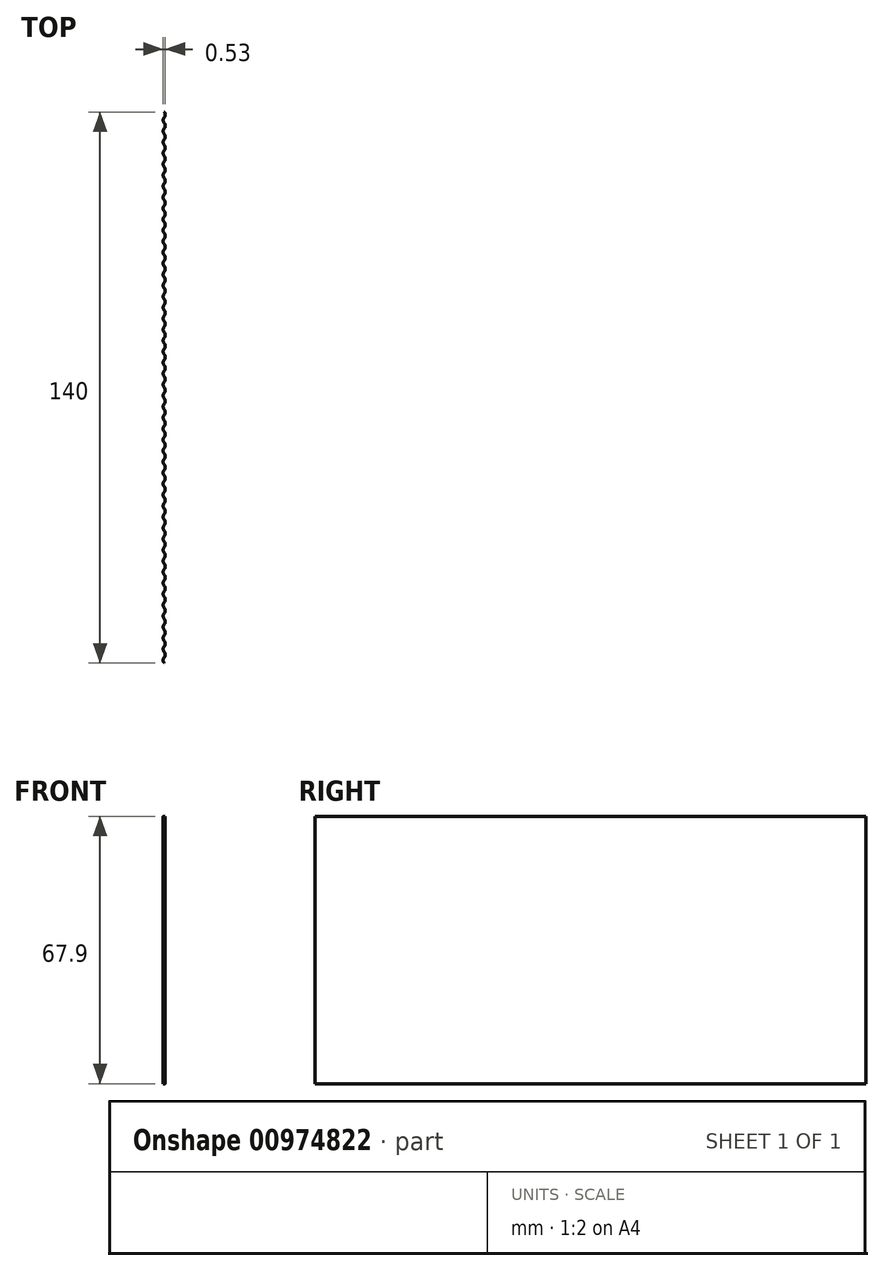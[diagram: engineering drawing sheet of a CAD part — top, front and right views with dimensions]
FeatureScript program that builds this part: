
annotation { "Feature Type Name" : "Feature", "Feature Type Description" : "" }
export const myFeature = defineFeature(function(context is Context, id is Id, definition is map)
    precondition{}
    {
        {
            var Q0;
            Q0=qCreatedBy(makeId("Top.planeOp"),FACE);
            var sketch = newSketch(context, id + "F0", { "sketchPlane" : qUnion([Q0])});
            skArc(sketch, "E0", {"start": v(0, 1.4) * mm, "mid": v(-0.25, 0.7) * mm, "end": v(0, 0) * mm});
            skArc(sketch, "E1", {"start": v(0, 1.4) * mm, "mid": v(0.25, 2.1) * mm, "end": v(0, 2.8) * mm});
            skArc(sketch, "E2.1.0.0", {"start": v(0.03, 1.4) * mm, "mid": v(0.28, 2.1) * mm, "end": v(0.03, 2.8) * mm});
            skArc(sketch, "E2.1.0.1", {"start": v(0.03, 1.4) * mm, "mid": v(-0.22, 0.7) * mm, "end": v(0.03, 0) * mm});
            skLineSegment(sketch, "E2.direction1", {"start": v(0, 0) * mm, "end": v(0.03, 0) * mm, "construction": true});
            skArc(sketch, "E3.0.1.0", {"start": v(0.03, 4.2) * mm, "mid": v(0.28, 4.9) * mm, "end": v(0.03, 5.6) * mm});
            skArc(sketch, "E3.0.1.1", {"start": v(0, 4.2) * mm, "mid": v(-0.25, 3.5) * mm, "end": v(0, 2.8) * mm});
            skArc(sketch, "E3.0.1.2", {"start": v(0.03, 4.2) * mm, "mid": v(-0.22, 3.5) * mm, "end": v(0.03, 2.8) * mm});
            skArc(sketch, "E3.0.1.3", {"start": v(0, 4.2) * mm, "mid": v(0.25, 4.9) * mm, "end": v(0, 5.6) * mm});
            skLineSegment(sketch, "E3.0.1.4", {"start": v(0, 2.8) * mm, "end": v(0.03, 2.8) * mm, "construction": true});
            skArc(sketch, "E3.0.2.0", {"start": v(0.03, 7) * mm, "mid": v(0.28, 7.7) * mm, "end": v(0.03, 8.4) * mm});
            skArc(sketch, "E3.0.2.1", {"start": v(0, 7) * mm, "mid": v(-0.25, 6.3) * mm, "end": v(0, 5.6) * mm});
            skArc(sketch, "E3.0.2.2", {"start": v(0.03, 7) * mm, "mid": v(-0.22, 6.3) * mm, "end": v(0.03, 5.6) * mm});
            skArc(sketch, "E3.0.2.3", {"start": v(0, 7) * mm, "mid": v(0.25, 7.7) * mm, "end": v(0, 8.4) * mm});
            skLineSegment(sketch, "E3.0.2.4", {"start": v(0, 5.6) * mm, "end": v(0.03, 5.6) * mm, "construction": true});
            skArc(sketch, "E3.0.3.0", {"start": v(0.03, 9.8) * mm, "mid": v(0.28, 10.5) * mm, "end": v(0.03, 11.2) * mm});
            skArc(sketch, "E3.0.3.1", {"start": v(0, 9.8) * mm, "mid": v(-0.25, 9.1) * mm, "end": v(0, 8.4) * mm});
            skArc(sketch, "E3.0.3.2", {"start": v(0.03, 9.8) * mm, "mid": v(-0.22, 9.1) * mm, "end": v(0.03, 8.4) * mm});
            skArc(sketch, "E3.0.3.3", {"start": v(0, 9.8) * mm, "mid": v(0.25, 10.5) * mm, "end": v(0, 11.2) * mm});
            skLineSegment(sketch, "E3.0.3.4", {"start": v(0, 8.4) * mm, "end": v(0.03, 8.4) * mm, "construction": true});
            skArc(sketch, "E3.0.4.0", {"start": v(0.03, 12.6) * mm, "mid": v(0.28, 13.3) * mm, "end": v(0.03, 14) * mm});
            skArc(sketch, "E3.0.4.1", {"start": v(0, 12.6) * mm, "mid": v(-0.25, 11.9) * mm, "end": v(0, 11.2) * mm});
            skArc(sketch, "E3.0.4.2", {"start": v(0.03, 12.6) * mm, "mid": v(-0.22, 11.9) * mm, "end": v(0.03, 11.2) * mm});
            skArc(sketch, "E3.0.4.3", {"start": v(0, 12.6) * mm, "mid": v(0.25, 13.3) * mm, "end": v(0, 14) * mm});
            skLineSegment(sketch, "E3.0.4.4", {"start": v(0, 11.2) * mm, "end": v(0.03, 11.2) * mm, "construction": true});
            skArc(sketch, "E3.0.5.0", {"start": v(0.03, 15.4) * mm, "mid": v(0.28, 16.1) * mm, "end": v(0.03, 16.8) * mm});
            skArc(sketch, "E3.0.5.1", {"start": v(0, 15.4) * mm, "mid": v(-0.25, 14.7) * mm, "end": v(0, 14) * mm});
            skArc(sketch, "E3.0.5.2", {"start": v(0.03, 15.4) * mm, "mid": v(-0.22, 14.7) * mm, "end": v(0.03, 14) * mm});
            skArc(sketch, "E3.0.5.3", {"start": v(0, 15.4) * mm, "mid": v(0.25, 16.1) * mm, "end": v(0, 16.8) * mm});
            skLineSegment(sketch, "E3.0.5.4", {"start": v(0, 14) * mm, "end": v(0.03, 14) * mm, "construction": true});
            skArc(sketch, "E3.0.6.0", {"start": v(0.03, 18.2) * mm, "mid": v(0.28, 18.9) * mm, "end": v(0.03, 19.6) * mm});
            skArc(sketch, "E3.0.6.1", {"start": v(0, 18.2) * mm, "mid": v(-0.25, 17.5) * mm, "end": v(0, 16.8) * mm});
            skArc(sketch, "E3.0.6.2", {"start": v(0.03, 18.2) * mm, "mid": v(-0.22, 17.5) * mm, "end": v(0.03, 16.8) * mm});
            skArc(sketch, "E3.0.6.3", {"start": v(0, 18.2) * mm, "mid": v(0.25, 18.9) * mm, "end": v(0, 19.6) * mm});
            skLineSegment(sketch, "E3.0.6.4", {"start": v(0, 16.8) * mm, "end": v(0.03, 16.8) * mm, "construction": true});
            skArc(sketch, "E3.0.7.0", {"start": v(0.03, 21) * mm, "mid": v(0.28, 21.7) * mm, "end": v(0.03, 22.4) * mm});
            skArc(sketch, "E3.0.7.1", {"start": v(0, 21) * mm, "mid": v(-0.25, 20.3) * mm, "end": v(0, 19.6) * mm});
            skArc(sketch, "E3.0.7.2", {"start": v(0.03, 21) * mm, "mid": v(-0.22, 20.3) * mm, "end": v(0.03, 19.6) * mm});
            skArc(sketch, "E3.0.7.3", {"start": v(0, 21) * mm, "mid": v(0.25, 21.7) * mm, "end": v(0, 22.4) * mm});
            skLineSegment(sketch, "E3.0.7.4", {"start": v(0, 19.6) * mm, "end": v(0.03, 19.6) * mm, "construction": true});
            skArc(sketch, "E3.0.8.0", {"start": v(0.03, 23.8) * mm, "mid": v(0.28, 24.5) * mm, "end": v(0.03, 25.2) * mm});
            skArc(sketch, "E3.0.8.1", {"start": v(0, 23.8) * mm, "mid": v(-0.25, 23.1) * mm, "end": v(0, 22.4) * mm});
            skArc(sketch, "E3.0.8.2", {"start": v(0.03, 23.8) * mm, "mid": v(-0.22, 23.1) * mm, "end": v(0.03, 22.4) * mm});
            skArc(sketch, "E3.0.8.3", {"start": v(0, 23.8) * mm, "mid": v(0.25, 24.5) * mm, "end": v(0, 25.2) * mm});
            skLineSegment(sketch, "E3.0.8.4", {"start": v(0, 22.4) * mm, "end": v(0.03, 22.4) * mm, "construction": true});
            skArc(sketch, "E3.0.9.0", {"start": v(0.03, 26.6) * mm, "mid": v(0.28, 27.3) * mm, "end": v(0.03, 28) * mm});
            skArc(sketch, "E3.0.9.1", {"start": v(0, 26.6) * mm, "mid": v(-0.25, 25.9) * mm, "end": v(0, 25.2) * mm});
            skArc(sketch, "E3.0.9.2", {"start": v(0.03, 26.6) * mm, "mid": v(-0.22, 25.9) * mm, "end": v(0.03, 25.2) * mm});
            skArc(sketch, "E3.0.9.3", {"start": v(0, 26.6) * mm, "mid": v(0.25, 27.3) * mm, "end": v(0, 28) * mm});
            skLineSegment(sketch, "E3.0.9.4", {"start": v(0, 25.2) * mm, "end": v(0.03, 25.2) * mm, "construction": true});
            skArc(sketch, "E3.0.10.0", {"start": v(0.03, 29.4) * mm, "mid": v(0.28, 30.1) * mm, "end": v(0.03, 30.8) * mm});
            skArc(sketch, "E3.0.10.1", {"start": v(0, 29.4) * mm, "mid": v(-0.25, 28.7) * mm, "end": v(0, 28) * mm});
            skArc(sketch, "E3.0.10.2", {"start": v(0.03, 29.4) * mm, "mid": v(-0.22, 28.7) * mm, "end": v(0.03, 28) * mm});
            skArc(sketch, "E3.0.10.3", {"start": v(0, 29.4) * mm, "mid": v(0.25, 30.1) * mm, "end": v(0, 30.8) * mm});
            skLineSegment(sketch, "E3.0.10.4", {"start": v(0, 28) * mm, "end": v(0.03, 28) * mm, "construction": true});
            skArc(sketch, "E3.0.11.0", {"start": v(0.03, 32.2) * mm, "mid": v(0.28, 32.9) * mm, "end": v(0.03, 33.6) * mm});
            skArc(sketch, "E3.0.11.1", {"start": v(0, 32.2) * mm, "mid": v(-0.25, 31.5) * mm, "end": v(0, 30.8) * mm});
            skArc(sketch, "E3.0.11.2", {"start": v(0.03, 32.2) * mm, "mid": v(-0.22, 31.5) * mm, "end": v(0.03, 30.8) * mm});
            skArc(sketch, "E3.0.11.3", {"start": v(0, 32.2) * mm, "mid": v(0.25, 32.9) * mm, "end": v(0, 33.6) * mm});
            skLineSegment(sketch, "E3.0.11.4", {"start": v(0, 30.8) * mm, "end": v(0.03, 30.8) * mm, "construction": true});
            skArc(sketch, "E3.0.12.0", {"start": v(0.03, 35) * mm, "mid": v(0.28, 35.7) * mm, "end": v(0.03, 36.4) * mm});
            skArc(sketch, "E3.0.12.1", {"start": v(0, 35) * mm, "mid": v(-0.25, 34.3) * mm, "end": v(0, 33.6) * mm});
            skArc(sketch, "E3.0.12.2", {"start": v(0.03, 35) * mm, "mid": v(-0.22, 34.3) * mm, "end": v(0.03, 33.6) * mm});
            skArc(sketch, "E3.0.12.3", {"start": v(0, 35) * mm, "mid": v(0.25, 35.7) * mm, "end": v(0, 36.4) * mm});
            skLineSegment(sketch, "E3.0.12.4", {"start": v(0, 33.6) * mm, "end": v(0.03, 33.6) * mm, "construction": true});
            skArc(sketch, "E3.0.13.0", {"start": v(0.03, 37.8) * mm, "mid": v(0.28, 38.5) * mm, "end": v(0.03, 39.2) * mm});
            skArc(sketch, "E3.0.13.1", {"start": v(0, 37.8) * mm, "mid": v(-0.25, 37.1) * mm, "end": v(0, 36.4) * mm});
            skArc(sketch, "E3.0.13.2", {"start": v(0.03, 37.8) * mm, "mid": v(-0.22, 37.1) * mm, "end": v(0.03, 36.4) * mm});
            skArc(sketch, "E3.0.13.3", {"start": v(0, 37.8) * mm, "mid": v(0.25, 38.5) * mm, "end": v(0, 39.2) * mm});
            skLineSegment(sketch, "E3.0.13.4", {"start": v(0, 36.4) * mm, "end": v(0.03, 36.4) * mm, "construction": true});
            skArc(sketch, "E3.0.14.0", {"start": v(0.03, 40.6) * mm, "mid": v(0.28, 41.3) * mm, "end": v(0.03, 42) * mm});
            skArc(sketch, "E3.0.14.1", {"start": v(0, 40.6) * mm, "mid": v(-0.25, 39.9) * mm, "end": v(0, 39.2) * mm});
            skArc(sketch, "E3.0.14.2", {"start": v(0.03, 40.6) * mm, "mid": v(-0.22, 39.9) * mm, "end": v(0.03, 39.2) * mm});
            skArc(sketch, "E3.0.14.3", {"start": v(0, 40.6) * mm, "mid": v(0.25, 41.3) * mm, "end": v(0, 42) * mm});
            skLineSegment(sketch, "E3.0.14.4", {"start": v(0, 39.2) * mm, "end": v(0.03, 39.2) * mm, "construction": true});
            skArc(sketch, "E3.0.15.0", {"start": v(0.03, 43.4) * mm, "mid": v(0.28, 44.1) * mm, "end": v(0.03, 44.8) * mm});
            skArc(sketch, "E3.0.15.1", {"start": v(0, 43.4) * mm, "mid": v(-0.25, 42.7) * mm, "end": v(0, 42) * mm});
            skArc(sketch, "E3.0.15.2", {"start": v(0.03, 43.4) * mm, "mid": v(-0.22, 42.7) * mm, "end": v(0.03, 42) * mm});
            skArc(sketch, "E3.0.15.3", {"start": v(0, 43.4) * mm, "mid": v(0.25, 44.1) * mm, "end": v(0, 44.8) * mm});
            skLineSegment(sketch, "E3.0.15.4", {"start": v(0, 42) * mm, "end": v(0.03, 42) * mm, "construction": true});
            skArc(sketch, "E3.0.16.0", {"start": v(0.03, 46.2) * mm, "mid": v(0.28, 46.9) * mm, "end": v(0.03, 47.6) * mm});
            skArc(sketch, "E3.0.16.1", {"start": v(0, 46.2) * mm, "mid": v(-0.25, 45.5) * mm, "end": v(0, 44.8) * mm});
            skArc(sketch, "E3.0.16.2", {"start": v(0.03, 46.2) * mm, "mid": v(-0.22, 45.5) * mm, "end": v(0.03, 44.8) * mm});
            skArc(sketch, "E3.0.16.3", {"start": v(0, 46.2) * mm, "mid": v(0.25, 46.9) * mm, "end": v(0, 47.6) * mm});
            skLineSegment(sketch, "E3.0.16.4", {"start": v(0, 44.8) * mm, "end": v(0.03, 44.8) * mm, "construction": true});
            skArc(sketch, "E3.0.17.0", {"start": v(0.03, 49) * mm, "mid": v(0.28, 49.7) * mm, "end": v(0.03, 50.4) * mm});
            skArc(sketch, "E3.0.17.1", {"start": v(0, 49) * mm, "mid": v(-0.25, 48.3) * mm, "end": v(0, 47.6) * mm});
            skArc(sketch, "E3.0.17.2", {"start": v(0.03, 49) * mm, "mid": v(-0.22, 48.3) * mm, "end": v(0.03, 47.6) * mm});
            skArc(sketch, "E3.0.17.3", {"start": v(0, 49) * mm, "mid": v(0.25, 49.7) * mm, "end": v(0, 50.4) * mm});
            skLineSegment(sketch, "E3.0.17.4", {"start": v(0, 47.6) * mm, "end": v(0.03, 47.6) * mm, "construction": true});
            skArc(sketch, "E3.0.18.0", {"start": v(0.03, 51.8) * mm, "mid": v(0.28, 52.5) * mm, "end": v(0.03, 53.2) * mm});
            skArc(sketch, "E3.0.18.1", {"start": v(0, 51.8) * mm, "mid": v(-0.25, 51.1) * mm, "end": v(0, 50.4) * mm});
            skArc(sketch, "E3.0.18.2", {"start": v(0.03, 51.8) * mm, "mid": v(-0.22, 51.1) * mm, "end": v(0.03, 50.4) * mm});
            skArc(sketch, "E3.0.18.3", {"start": v(0, 51.8) * mm, "mid": v(0.25, 52.5) * mm, "end": v(0, 53.2) * mm});
            skLineSegment(sketch, "E3.0.18.4", {"start": v(0, 50.4) * mm, "end": v(0.03, 50.4) * mm, "construction": true});
            skArc(sketch, "E3.0.19.0", {"start": v(0.03, 54.6) * mm, "mid": v(0.28, 55.3) * mm, "end": v(0.03, 56) * mm});
            skArc(sketch, "E3.0.19.1", {"start": v(0, 54.6) * mm, "mid": v(-0.25, 53.9) * mm, "end": v(0, 53.2) * mm});
            skArc(sketch, "E3.0.19.2", {"start": v(0.03, 54.6) * mm, "mid": v(-0.22, 53.9) * mm, "end": v(0.03, 53.2) * mm});
            skArc(sketch, "E3.0.19.3", {"start": v(0, 54.6) * mm, "mid": v(0.25, 55.3) * mm, "end": v(0, 56) * mm});
            skLineSegment(sketch, "E3.0.19.4", {"start": v(0, 53.2) * mm, "end": v(0.03, 53.2) * mm, "construction": true});
            skArc(sketch, "E3.0.20.0", {"start": v(0.03, 57.4) * mm, "mid": v(0.28, 58.1) * mm, "end": v(0.03, 58.8) * mm});
            skArc(sketch, "E3.0.20.1", {"start": v(0, 57.4) * mm, "mid": v(-0.25, 56.7) * mm, "end": v(0, 56) * mm});
            skArc(sketch, "E3.0.20.2", {"start": v(0.03, 57.4) * mm, "mid": v(-0.22, 56.7) * mm, "end": v(0.03, 56) * mm});
            skArc(sketch, "E3.0.20.3", {"start": v(0, 57.4) * mm, "mid": v(0.25, 58.1) * mm, "end": v(0, 58.8) * mm});
            skLineSegment(sketch, "E3.0.20.4", {"start": v(0, 56) * mm, "end": v(0.03, 56) * mm, "construction": true});
            skArc(sketch, "E3.0.21.0", {"start": v(0.03, 60.2) * mm, "mid": v(0.28, 60.9) * mm, "end": v(0.03, 61.6) * mm});
            skArc(sketch, "E3.0.21.1", {"start": v(0, 60.2) * mm, "mid": v(-0.25, 59.5) * mm, "end": v(0, 58.8) * mm});
            skArc(sketch, "E3.0.21.2", {"start": v(0.03, 60.2) * mm, "mid": v(-0.22, 59.5) * mm, "end": v(0.03, 58.8) * mm});
            skArc(sketch, "E3.0.21.3", {"start": v(0, 60.2) * mm, "mid": v(0.25, 60.9) * mm, "end": v(0, 61.6) * mm});
            skLineSegment(sketch, "E3.0.21.4", {"start": v(0, 58.8) * mm, "end": v(0.03, 58.8) * mm, "construction": true});
            skArc(sketch, "E3.0.22.0", {"start": v(0.03, 63) * mm, "mid": v(0.28, 63.7) * mm, "end": v(0.03, 64.4) * mm});
            skArc(sketch, "E3.0.22.1", {"start": v(0, 63) * mm, "mid": v(-0.25, 62.3) * mm, "end": v(0, 61.6) * mm});
            skArc(sketch, "E3.0.22.2", {"start": v(0.03, 63) * mm, "mid": v(-0.22, 62.3) * mm, "end": v(0.03, 61.6) * mm});
            skArc(sketch, "E3.0.22.3", {"start": v(0, 63) * mm, "mid": v(0.25, 63.7) * mm, "end": v(0, 64.4) * mm});
            skLineSegment(sketch, "E3.0.22.4", {"start": v(0, 61.6) * mm, "end": v(0.03, 61.6) * mm, "construction": true});
            skArc(sketch, "E3.0.23.0", {"start": v(0.03, 65.8) * mm, "mid": v(0.28, 66.5) * mm, "end": v(0.03, 67.2) * mm});
            skArc(sketch, "E3.0.23.1", {"start": v(0, 65.8) * mm, "mid": v(-0.25, 65.1) * mm, "end": v(0, 64.4) * mm});
            skArc(sketch, "E3.0.23.2", {"start": v(0.03, 65.8) * mm, "mid": v(-0.22, 65.1) * mm, "end": v(0.03, 64.4) * mm});
            skArc(sketch, "E3.0.23.3", {"start": v(0, 65.8) * mm, "mid": v(0.25, 66.5) * mm, "end": v(0, 67.2) * mm});
            skLineSegment(sketch, "E3.0.23.4", {"start": v(0, 64.4) * mm, "end": v(0.03, 64.4) * mm, "construction": true});
            skArc(sketch, "E3.0.24.0", {"start": v(0.03, 68.6) * mm, "mid": v(0.28, 69.3) * mm, "end": v(0.03, 70) * mm});
            skArc(sketch, "E3.0.24.1", {"start": v(0, 68.6) * mm, "mid": v(-0.25, 67.9) * mm, "end": v(0, 67.2) * mm});
            skArc(sketch, "E3.0.24.2", {"start": v(0.03, 68.6) * mm, "mid": v(-0.22, 67.9) * mm, "end": v(0.03, 67.2) * mm});
            skArc(sketch, "E3.0.24.3", {"start": v(0, 68.6) * mm, "mid": v(0.25, 69.3) * mm, "end": v(0, 70) * mm});
            skLineSegment(sketch, "E3.0.24.4", {"start": v(0, 67.2) * mm, "end": v(0.03, 67.2) * mm, "construction": true});
            skArc(sketch, "E3.0.25.0", {"start": v(0.03, 71.4) * mm, "mid": v(0.28, 72.1) * mm, "end": v(0.03, 72.8) * mm});
            skArc(sketch, "E3.0.25.1", {"start": v(0, 71.4) * mm, "mid": v(-0.25, 70.7) * mm, "end": v(0, 70) * mm});
            skArc(sketch, "E3.0.25.2", {"start": v(0.03, 71.4) * mm, "mid": v(-0.22, 70.7) * mm, "end": v(0.03, 70) * mm});
            skArc(sketch, "E3.0.25.3", {"start": v(0, 71.4) * mm, "mid": v(0.25, 72.1) * mm, "end": v(0, 72.8) * mm});
            skLineSegment(sketch, "E3.0.25.4", {"start": v(0, 70) * mm, "end": v(0.03, 70) * mm, "construction": true});
            skArc(sketch, "E3.0.26.0", {"start": v(0.03, 74.2) * mm, "mid": v(0.28, 74.9) * mm, "end": v(0.03, 75.6) * mm});
            skArc(sketch, "E3.0.26.1", {"start": v(0, 74.2) * mm, "mid": v(-0.25, 73.5) * mm, "end": v(0, 72.8) * mm});
            skArc(sketch, "E3.0.26.2", {"start": v(0.03, 74.2) * mm, "mid": v(-0.22, 73.5) * mm, "end": v(0.03, 72.8) * mm});
            skArc(sketch, "E3.0.26.3", {"start": v(0, 74.2) * mm, "mid": v(0.25, 74.9) * mm, "end": v(0, 75.6) * mm});
            skLineSegment(sketch, "E3.0.26.4", {"start": v(0, 72.8) * mm, "end": v(0.03, 72.8) * mm, "construction": true});
            skArc(sketch, "E3.0.27.0", {"start": v(0.03, 77) * mm, "mid": v(0.28, 77.7) * mm, "end": v(0.03, 78.4) * mm});
            skArc(sketch, "E3.0.27.1", {"start": v(0, 77) * mm, "mid": v(-0.25, 76.3) * mm, "end": v(0, 75.6) * mm});
            skArc(sketch, "E3.0.27.2", {"start": v(0.03, 77) * mm, "mid": v(-0.22, 76.3) * mm, "end": v(0.03, 75.6) * mm});
            skArc(sketch, "E3.0.27.3", {"start": v(0, 77) * mm, "mid": v(0.25, 77.7) * mm, "end": v(0, 78.4) * mm});
            skLineSegment(sketch, "E3.0.27.4", {"start": v(0, 75.6) * mm, "end": v(0.03, 75.6) * mm, "construction": true});
            skArc(sketch, "E3.0.28.0", {"start": v(0.03, 79.8) * mm, "mid": v(0.28, 80.5) * mm, "end": v(0.03, 81.2) * mm});
            skArc(sketch, "E3.0.28.1", {"start": v(0, 79.8) * mm, "mid": v(-0.25, 79.1) * mm, "end": v(0, 78.4) * mm});
            skArc(sketch, "E3.0.28.2", {"start": v(0.03, 79.8) * mm, "mid": v(-0.22, 79.1) * mm, "end": v(0.03, 78.4) * mm});
            skArc(sketch, "E3.0.28.3", {"start": v(0, 79.8) * mm, "mid": v(0.25, 80.5) * mm, "end": v(0, 81.2) * mm});
            skLineSegment(sketch, "E3.0.28.4", {"start": v(0, 78.4) * mm, "end": v(0.03, 78.4) * mm, "construction": true});
            skArc(sketch, "E3.0.29.0", {"start": v(0.03, 82.6) * mm, "mid": v(0.28, 83.3) * mm, "end": v(0.03, 84) * mm});
            skArc(sketch, "E3.0.29.1", {"start": v(0, 82.6) * mm, "mid": v(-0.25, 81.9) * mm, "end": v(0, 81.2) * mm});
            skArc(sketch, "E3.0.29.2", {"start": v(0.03, 82.6) * mm, "mid": v(-0.22, 81.9) * mm, "end": v(0.03, 81.2) * mm});
            skArc(sketch, "E3.0.29.3", {"start": v(0, 82.6) * mm, "mid": v(0.25, 83.3) * mm, "end": v(0, 84) * mm});
            skLineSegment(sketch, "E3.0.29.4", {"start": v(0, 81.2) * mm, "end": v(0.03, 81.2) * mm, "construction": true});
            skArc(sketch, "E3.0.30.0", {"start": v(0.03, 85.4) * mm, "mid": v(0.28, 86.1) * mm, "end": v(0.03, 86.8) * mm});
            skArc(sketch, "E3.0.30.1", {"start": v(0, 85.4) * mm, "mid": v(-0.25, 84.7) * mm, "end": v(0, 84) * mm});
            skArc(sketch, "E3.0.30.2", {"start": v(0.03, 85.4) * mm, "mid": v(-0.22, 84.7) * mm, "end": v(0.03, 84) * mm});
            skArc(sketch, "E3.0.30.3", {"start": v(0, 85.4) * mm, "mid": v(0.25, 86.1) * mm, "end": v(0, 86.8) * mm});
            skLineSegment(sketch, "E3.0.30.4", {"start": v(0, 84) * mm, "end": v(0.03, 84) * mm, "construction": true});
            skArc(sketch, "E3.0.31.0", {"start": v(0.03, 88.2) * mm, "mid": v(0.28, 88.9) * mm, "end": v(0.03, 89.6) * mm});
            skArc(sketch, "E3.0.31.1", {"start": v(0, 88.2) * mm, "mid": v(-0.25, 87.5) * mm, "end": v(0, 86.8) * mm});
            skArc(sketch, "E3.0.31.2", {"start": v(0.03, 88.2) * mm, "mid": v(-0.22, 87.5) * mm, "end": v(0.03, 86.8) * mm});
            skArc(sketch, "E3.0.31.3", {"start": v(0, 88.2) * mm, "mid": v(0.25, 88.9) * mm, "end": v(0, 89.6) * mm});
            skLineSegment(sketch, "E3.0.31.4", {"start": v(0, 86.8) * mm, "end": v(0.03, 86.8) * mm, "construction": true});
            skArc(sketch, "E3.0.32.0", {"start": v(0.03, 91) * mm, "mid": v(0.28, 91.7) * mm, "end": v(0.03, 92.4) * mm});
            skArc(sketch, "E3.0.32.1", {"start": v(0, 91) * mm, "mid": v(-0.25, 90.3) * mm, "end": v(0, 89.6) * mm});
            skArc(sketch, "E3.0.32.2", {"start": v(0.03, 91) * mm, "mid": v(-0.22, 90.3) * mm, "end": v(0.03, 89.6) * mm});
            skArc(sketch, "E3.0.32.3", {"start": v(0, 91) * mm, "mid": v(0.25, 91.7) * mm, "end": v(0, 92.4) * mm});
            skLineSegment(sketch, "E3.0.32.4", {"start": v(0, 89.6) * mm, "end": v(0.03, 89.6) * mm, "construction": true});
            skArc(sketch, "E3.0.33.0", {"start": v(0.03, 93.8) * mm, "mid": v(0.28, 94.5) * mm, "end": v(0.03, 95.2) * mm});
            skArc(sketch, "E3.0.33.1", {"start": v(0, 93.8) * mm, "mid": v(-0.25, 93.1) * mm, "end": v(0, 92.4) * mm});
            skArc(sketch, "E3.0.33.2", {"start": v(0.03, 93.8) * mm, "mid": v(-0.22, 93.1) * mm, "end": v(0.03, 92.4) * mm});
            skArc(sketch, "E3.0.33.3", {"start": v(0, 93.8) * mm, "mid": v(0.25, 94.5) * mm, "end": v(0, 95.2) * mm});
            skLineSegment(sketch, "E3.0.33.4", {"start": v(0, 92.4) * mm, "end": v(0.03, 92.4) * mm, "construction": true});
            skArc(sketch, "E3.0.34.0", {"start": v(0.03, 96.6) * mm, "mid": v(0.28, 97.3) * mm, "end": v(0.03, 98) * mm});
            skArc(sketch, "E3.0.34.1", {"start": v(0, 96.6) * mm, "mid": v(-0.25, 95.9) * mm, "end": v(0, 95.2) * mm});
            skArc(sketch, "E3.0.34.2", {"start": v(0.03, 96.6) * mm, "mid": v(-0.22, 95.9) * mm, "end": v(0.03, 95.2) * mm});
            skArc(sketch, "E3.0.34.3", {"start": v(0, 96.6) * mm, "mid": v(0.25, 97.3) * mm, "end": v(0, 98) * mm});
            skLineSegment(sketch, "E3.0.34.4", {"start": v(0, 95.2) * mm, "end": v(0.03, 95.2) * mm, "construction": true});
            skArc(sketch, "E3.0.35.0", {"start": v(0.03, 99.4) * mm, "mid": v(0.28, 100.1) * mm, "end": v(0.03, 100.8) * mm});
            skArc(sketch, "E3.0.35.1", {"start": v(0, 99.4) * mm, "mid": v(-0.25, 98.7) * mm, "end": v(0, 98) * mm});
            skArc(sketch, "E3.0.35.2", {"start": v(0.03, 99.4) * mm, "mid": v(-0.22, 98.7) * mm, "end": v(0.03, 98) * mm});
            skArc(sketch, "E3.0.35.3", {"start": v(0, 99.4) * mm, "mid": v(0.25, 100.1) * mm, "end": v(0, 100.8) * mm});
            skLineSegment(sketch, "E3.0.35.4", {"start": v(0, 98) * mm, "end": v(0.03, 98) * mm, "construction": true});
            skArc(sketch, "E3.0.36.0", {"start": v(0.03, 102.2) * mm, "mid": v(0.28, 102.9) * mm, "end": v(0.03, 103.6) * mm});
            skArc(sketch, "E3.0.36.1", {"start": v(0, 102.2) * mm, "mid": v(-0.25, 101.5) * mm, "end": v(0, 100.8) * mm});
            skArc(sketch, "E3.0.36.2", {"start": v(0.03, 102.2) * mm, "mid": v(-0.22, 101.5) * mm, "end": v(0.03, 100.8) * mm});
            skArc(sketch, "E3.0.36.3", {"start": v(0, 102.2) * mm, "mid": v(0.25, 102.9) * mm, "end": v(0, 103.6) * mm});
            skLineSegment(sketch, "E3.0.36.4", {"start": v(0, 100.8) * mm, "end": v(0.03, 100.8) * mm, "construction": true});
            skArc(sketch, "E3.0.37.0", {"start": v(0.03, 105) * mm, "mid": v(0.28, 105.7) * mm, "end": v(0.03, 106.4) * mm});
            skArc(sketch, "E3.0.37.1", {"start": v(0, 105) * mm, "mid": v(-0.25, 104.3) * mm, "end": v(0, 103.6) * mm});
            skArc(sketch, "E3.0.37.2", {"start": v(0.03, 105) * mm, "mid": v(-0.22, 104.3) * mm, "end": v(0.03, 103.6) * mm});
            skArc(sketch, "E3.0.37.3", {"start": v(0, 105) * mm, "mid": v(0.25, 105.7) * mm, "end": v(0, 106.4) * mm});
            skLineSegment(sketch, "E3.0.37.4", {"start": v(0, 103.6) * mm, "end": v(0.03, 103.6) * mm, "construction": true});
            skArc(sketch, "E3.0.38.0", {"start": v(0.03, 107.8) * mm, "mid": v(0.28, 108.5) * mm, "end": v(0.03, 109.2) * mm});
            skArc(sketch, "E3.0.38.1", {"start": v(0, 107.8) * mm, "mid": v(-0.25, 107.1) * mm, "end": v(0, 106.4) * mm});
            skArc(sketch, "E3.0.38.2", {"start": v(0.03, 107.8) * mm, "mid": v(-0.22, 107.1) * mm, "end": v(0.03, 106.4) * mm});
            skArc(sketch, "E3.0.38.3", {"start": v(0, 107.8) * mm, "mid": v(0.25, 108.5) * mm, "end": v(0, 109.2) * mm});
            skLineSegment(sketch, "E3.0.38.4", {"start": v(0, 106.4) * mm, "end": v(0.03, 106.4) * mm, "construction": true});
            skArc(sketch, "E3.0.39.0", {"start": v(0.03, 110.6) * mm, "mid": v(0.28, 111.3) * mm, "end": v(0.03, 112) * mm});
            skArc(sketch, "E3.0.39.1", {"start": v(0, 110.6) * mm, "mid": v(-0.25, 109.9) * mm, "end": v(0, 109.2) * mm});
            skArc(sketch, "E3.0.39.2", {"start": v(0.03, 110.6) * mm, "mid": v(-0.22, 109.9) * mm, "end": v(0.03, 109.2) * mm});
            skArc(sketch, "E3.0.39.3", {"start": v(0, 110.6) * mm, "mid": v(0.25, 111.3) * mm, "end": v(0, 112) * mm});
            skLineSegment(sketch, "E3.0.39.4", {"start": v(0, 109.2) * mm, "end": v(0.03, 109.2) * mm, "construction": true});
            skArc(sketch, "E3.0.40.0", {"start": v(0.03, 113.4) * mm, "mid": v(0.28, 114.1) * mm, "end": v(0.03, 114.8) * mm});
            skArc(sketch, "E3.0.40.1", {"start": v(0, 113.4) * mm, "mid": v(-0.25, 112.7) * mm, "end": v(0, 112) * mm});
            skArc(sketch, "E3.0.40.2", {"start": v(0.03, 113.4) * mm, "mid": v(-0.22, 112.7) * mm, "end": v(0.03, 112) * mm});
            skArc(sketch, "E3.0.40.3", {"start": v(0, 113.4) * mm, "mid": v(0.25, 114.1) * mm, "end": v(0, 114.8) * mm});
            skLineSegment(sketch, "E3.0.40.4", {"start": v(0, 112) * mm, "end": v(0.03, 112) * mm, "construction": true});
            skArc(sketch, "E3.0.41.0", {"start": v(0.03, 116.2) * mm, "mid": v(0.28, 116.9) * mm, "end": v(0.03, 117.6) * mm});
            skArc(sketch, "E3.0.41.1", {"start": v(0, 116.2) * mm, "mid": v(-0.25, 115.5) * mm, "end": v(0, 114.8) * mm});
            skArc(sketch, "E3.0.41.2", {"start": v(0.03, 116.2) * mm, "mid": v(-0.22, 115.5) * mm, "end": v(0.03, 114.8) * mm});
            skArc(sketch, "E3.0.41.3", {"start": v(0, 116.2) * mm, "mid": v(0.25, 116.9) * mm, "end": v(0, 117.6) * mm});
            skLineSegment(sketch, "E3.0.41.4", {"start": v(0, 114.8) * mm, "end": v(0.03, 114.8) * mm, "construction": true});
            skArc(sketch, "E3.0.42.0", {"start": v(0.03, 119) * mm, "mid": v(0.28, 119.7) * mm, "end": v(0.03, 120.4) * mm});
            skArc(sketch, "E3.0.42.1", {"start": v(0, 119) * mm, "mid": v(-0.25, 118.3) * mm, "end": v(0, 117.6) * mm});
            skArc(sketch, "E3.0.42.2", {"start": v(0.03, 119) * mm, "mid": v(-0.22, 118.3) * mm, "end": v(0.03, 117.6) * mm});
            skArc(sketch, "E3.0.42.3", {"start": v(0, 119) * mm, "mid": v(0.25, 119.7) * mm, "end": v(0, 120.4) * mm});
            skLineSegment(sketch, "E3.0.42.4", {"start": v(0, 117.6) * mm, "end": v(0.03, 117.6) * mm, "construction": true});
            skArc(sketch, "E3.0.43.0", {"start": v(0.03, 121.8) * mm, "mid": v(0.28, 122.5) * mm, "end": v(0.03, 123.2) * mm});
            skArc(sketch, "E3.0.43.1", {"start": v(0, 121.8) * mm, "mid": v(-0.25, 121.1) * mm, "end": v(0, 120.4) * mm});
            skArc(sketch, "E3.0.43.2", {"start": v(0.03, 121.8) * mm, "mid": v(-0.22, 121.1) * mm, "end": v(0.03, 120.4) * mm});
            skArc(sketch, "E3.0.43.3", {"start": v(0, 121.8) * mm, "mid": v(0.25, 122.5) * mm, "end": v(0, 123.2) * mm});
            skLineSegment(sketch, "E3.0.43.4", {"start": v(0, 120.4) * mm, "end": v(0.03, 120.4) * mm, "construction": true});
            skArc(sketch, "E3.0.44.0", {"start": v(0.03, 124.6) * mm, "mid": v(0.28, 125.3) * mm, "end": v(0.03, 126) * mm});
            skArc(sketch, "E3.0.44.1", {"start": v(0, 124.6) * mm, "mid": v(-0.25, 123.9) * mm, "end": v(0, 123.2) * mm});
            skArc(sketch, "E3.0.44.2", {"start": v(0.03, 124.6) * mm, "mid": v(-0.22, 123.9) * mm, "end": v(0.03, 123.2) * mm});
            skArc(sketch, "E3.0.44.3", {"start": v(0, 124.6) * mm, "mid": v(0.25, 125.3) * mm, "end": v(0, 126) * mm});
            skLineSegment(sketch, "E3.0.44.4", {"start": v(0, 123.2) * mm, "end": v(0.03, 123.2) * mm, "construction": true});
            skArc(sketch, "E3.0.45.0", {"start": v(0.03, 127.4) * mm, "mid": v(0.28, 128.1) * mm, "end": v(0.03, 128.8) * mm});
            skArc(sketch, "E3.0.45.1", {"start": v(0, 127.4) * mm, "mid": v(-0.25, 126.7) * mm, "end": v(0, 126) * mm});
            skArc(sketch, "E3.0.45.2", {"start": v(0.03, 127.4) * mm, "mid": v(-0.22, 126.7) * mm, "end": v(0.03, 126) * mm});
            skArc(sketch, "E3.0.45.3", {"start": v(0, 127.4) * mm, "mid": v(0.25, 128.1) * mm, "end": v(0, 128.8) * mm});
            skLineSegment(sketch, "E3.0.45.4", {"start": v(0, 126) * mm, "end": v(0.03, 126) * mm, "construction": true});
            skArc(sketch, "E3.0.46.0", {"start": v(0.03, 130.2) * mm, "mid": v(0.28, 130.9) * mm, "end": v(0.03, 131.6) * mm});
            skArc(sketch, "E3.0.46.1", {"start": v(0, 130.2) * mm, "mid": v(-0.25, 129.5) * mm, "end": v(0, 128.8) * mm});
            skArc(sketch, "E3.0.46.2", {"start": v(0.03, 130.2) * mm, "mid": v(-0.22, 129.5) * mm, "end": v(0.03, 128.8) * mm});
            skArc(sketch, "E3.0.46.3", {"start": v(0, 130.2) * mm, "mid": v(0.25, 130.9) * mm, "end": v(0, 131.6) * mm});
            skLineSegment(sketch, "E3.0.46.4", {"start": v(0, 128.8) * mm, "end": v(0.03, 128.8) * mm, "construction": true});
            skArc(sketch, "E3.0.47.0", {"start": v(0.03, 133) * mm, "mid": v(0.28, 133.7) * mm, "end": v(0.03, 134.4) * mm});
            skArc(sketch, "E3.0.47.1", {"start": v(0, 133) * mm, "mid": v(-0.25, 132.3) * mm, "end": v(0, 131.6) * mm});
            skArc(sketch, "E3.0.47.2", {"start": v(0.03, 133) * mm, "mid": v(-0.22, 132.3) * mm, "end": v(0.03, 131.6) * mm});
            skArc(sketch, "E3.0.47.3", {"start": v(0, 133) * mm, "mid": v(0.25, 133.7) * mm, "end": v(0, 134.4) * mm});
            skLineSegment(sketch, "E3.0.47.4", {"start": v(0, 131.6) * mm, "end": v(0.03, 131.6) * mm, "construction": true});
            skArc(sketch, "E3.0.48.0", {"start": v(0.03, 135.8) * mm, "mid": v(0.28, 136.5) * mm, "end": v(0.03, 137.2) * mm});
            skArc(sketch, "E3.0.48.1", {"start": v(0, 135.8) * mm, "mid": v(-0.25, 135.1) * mm, "end": v(0, 134.4) * mm});
            skArc(sketch, "E3.0.48.2", {"start": v(0.03, 135.8) * mm, "mid": v(-0.22, 135.1) * mm, "end": v(0.03, 134.4) * mm});
            skArc(sketch, "E3.0.48.3", {"start": v(0, 135.8) * mm, "mid": v(0.25, 136.5) * mm, "end": v(0, 137.2) * mm});
            skLineSegment(sketch, "E3.0.48.4", {"start": v(0, 134.4) * mm, "end": v(0.03, 134.4) * mm, "construction": true});
            skArc(sketch, "E3.0.49.0", {"start": v(0.03, 138.6) * mm, "mid": v(0.28, 139.3) * mm, "end": v(0.03, 140) * mm});
            skArc(sketch, "E3.0.49.1", {"start": v(0, 138.6) * mm, "mid": v(-0.25, 137.9) * mm, "end": v(0, 137.2) * mm});
            skArc(sketch, "E3.0.49.2", {"start": v(0.03, 138.6) * mm, "mid": v(-0.22, 137.9) * mm, "end": v(0.03, 137.2) * mm});
            skArc(sketch, "E3.0.49.3", {"start": v(0, 138.6) * mm, "mid": v(0.25, 139.3) * mm, "end": v(0, 140) * mm});
            skLineSegment(sketch, "E3.0.49.4", {"start": v(0, 137.2) * mm, "end": v(0.03, 137.2) * mm, "construction": true});
            skLineSegment(sketch, "E3.direction1", {"start": v(0, 0) * mm, "end": v(25, 0) * mm, "construction": true});
            skLineSegment(sketch, "E3.direction2", {"start": v(0, 0) * mm, "end": v(0, 2.8) * mm, "construction": true});
            skLineSegment(sketch, "E4", {"start": v(0, 0) * mm, "end": v(0.03, 0) * mm});
            skLineSegment(sketch, "E5", {"start": v(0, 140) * mm, "end": v(0.03, 140) * mm});
            skSolve(sketch);
        }
        {
            var Q0;
            Q0 = qSketchRegion(id + "F0", true);
            extrude(context, id + "F1", {"entities" : qUnion([Q0]), "depth" : 67.9 * mm, "offsetDistance" : 25 * mm});
        }
    });
